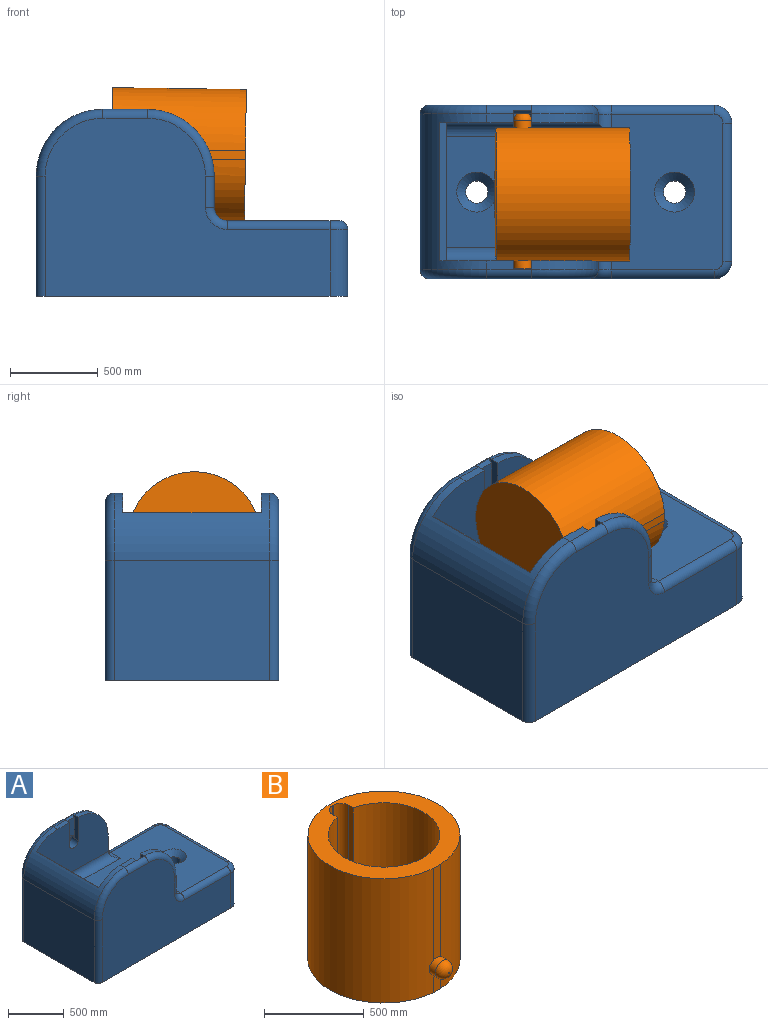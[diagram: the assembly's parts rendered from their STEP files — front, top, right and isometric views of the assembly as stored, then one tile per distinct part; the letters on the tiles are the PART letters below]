
ASSEMBLY  parts=2 mates=1
PART A: 60 faces, bbox 1817.8x1007.3x1098.2 mm
  f0: cylinder r=381mm len=380.99mm, axis (0,-1,0), area 30273.4mm2, adj f9,f10,f27,f48
  f1: plane 149.86x50.8mm, normal (0,0,1), area 7612.9mm2, adj f12,f14,f21,f47
  f2: cylinder r=381mm len=380.99mm, axis (0,-1,0), area 30273.4mm2, adj f12,f13,f22,f49
  f3: plane 1600.2x889mm, normal (0,0,1), area 1094222.8mm2, adj f33,f34,f35,f36,f37,f40,f41,f54
  f4: plane 889x685.8mm, normal (-1,0,0), area 609676.2mm2, adj f8,f14,f42,f43
  f5: plane 1625.6x1016mm, normal (0,-1,0), area 1156662mm2, adj f8,f38,f42,f44,f46,f48,f50,f52
  f6: plane 787.4x381mm, normal (1,0,0), area 299999.4mm2, adj f8,f38,f39,f58
  f7: plane 1625.6x1016mm, normal (0,1,0), area 1156662mm2, adj f8,f39,f43,f45,f47,f49,f51,f53
  f8: plane 1778x990.6mm, normal (0,0,-1), area 1730413.3mm2, adj f4,f5,f6,f7,f19,f20,f38,f39
  f9: plane 965.2x558.8mm, normal (0,1,0), area 450495.6mm2, adj f0,f10,f11,f14,f26,f27,f30,f31
  f10: plane 177.8x50.8mm, normal (1,0,0), area 9032.2mm2, adj f0,f9,f33,f50
  f11: plane 149.86x50.8mm, normal (0,0,1), area 7612.9mm2, adj f9,f14,f26,f46
  f12: plane 965.2x558.8mm, normal (0,-1,0), area 450606.9mm2, adj f1,f2,f13,f14,f17,f21,f22,f30
  f13: plane 177.8x50.8mm, normal (1,0,0), area 9032.2mm2, adj f2,f12,f34,f51
  f14: cylinder r=381mm len=889mm, axis (0,1,0), area 296423.9mm2, adj f1,f4,f9,f11,f12,f32,f44,f45
  f15: cylinder r=53.34mm len=106.68mm, axis (0,1,0), area 12769mm2, adj f16,f28,f29
  f16: plane 106.68x106.68mm, normal (0,1,0), area 8938.3mm2, adj f15
  f17: cylinder r=53.34mm len=106.68mm, axis (0,-1,0), area 21281.7mm2, adj f12,f18,f21,f22,f23
  f18: plane 106.68x106.68mm, normal (0,-1,0), area 8938.3mm2, adj f17
  f19: cylinder r=63.5mm len=381mm, axis (0,0,1), area 152012.2mm2, adj f8,f41
  f20: cylinder r=63.5mm len=381mm, axis (0,0,1), area 152012.2mm2, adj f8,f40
  f21: plane 254x71.7mm, normal (1,0,0), area 13184.9mm2, adj f1,f12,f17,f23,f25,f47
  f22: plane 254x71.71mm, normal (-1,0,0), area 13184.5mm2, adj f2,f12,f17,f23,f24,f49
  f23: plane 228.6x106.68mm, normal (0,-1,0), area 19917.9mm2, adj f17,f21,f22,f24,f25
  f24: cone r=355.6mm half-angle=45deg, axis (0,1,0), area 75.1mm2, adj f22,f23,f25,f49
  f25: plane 104.14x20.9mm, normal (0,-0.71,0.71), area 3078.2mm2, adj f21,f23,f24,f47
  f26: plane 255.04x50.8mm, normal (1,0,0), area 12956.2mm2, adj f9,f11,f28,f29,f59
  f27: plane 255.03x50.8mm, normal (-1,0,0), area 12955.7mm2, adj f0,f9,f28,f29,f59
  f28: plane 254x106.68mm, normal (0,1,0), area 22627.6mm2, adj f15,f26,f27,f46,f48
  f29: plane 106.68x54.38mm, normal (0,1,0), area 111.2mm2, adj f15,f26,f27,f59
  f30: plane 787.4x177.8mm, normal (1,0,0), area 139999.7mm2, adj f9,f12,f31,f37
  f31: cylinder r=330.34mm len=787.4mm, axis (0,1,0), area 205697.3mm2, adj f9,f12,f30,f32
  f32: plane 787.4x37.23mm, normal (0.68,0,0.73), area 39999.9mm2, adj f9,f12,f14,f31
  f33: cylinder r=76.2mm len=127mm, axis (0,1,0), area 9394.8mm2, adj f3,f10,f35,f52
  f34: cylinder r=76.2mm len=127mm, axis (0,1,0), area 9394.8mm2, adj f3,f13,f36,f53
  f35: cylinder r=76.2mm len=1041.4mm, axis (-1,0,0), area 115529.3mm2, adj f3,f9,f33,f37
  f36: cylinder r=76.2mm len=1041.4mm, axis (1,0,0), area 115529.3mm2, adj f3,f12,f34,f37
  f37: cylinder r=76.2mm len=787.4mm, axis (0,1,0), area 87619mm2, adj f3,f30,f35,f36
  f38: cylinder r=101.6mm len=381mm, axis (0,0,-1), area 60804.9mm2, adj f5,f6,f8,f56
  f39: cylinder r=101.6mm len=381mm, axis (0,0,1), area 60804.9mm2, adj f6,f7,f8,f57
  f40: cone r=63.5mm half-angle=45deg, axis (0,0,1), area 40129.2mm2, adj f3,f20
  f41: cone r=63.5mm half-angle=45deg, axis (0,0,1), area 40129.2mm2, adj f3,f19
  f42: cylinder r=50.8mm len=685.8mm, axis (0,0,1), area 54724.4mm2, adj f4,f5,f8,f44
  f43: cylinder r=50.8mm len=685.8mm, axis (0,0,-1), area 54724.4mm2, adj f4,f7,f8,f45
  f44: torus R=330.2mm, axis (0,1,0), area 45442.2mm2, adj f5,f14,f42,f46
  f45: torus R=330.2mm, axis (0,1,0), area 45442.2mm2, adj f7,f14,f43,f47
  f46: cylinder r=50.8mm len=254mm, axis (-1,0,0), area 20268.3mm2, adj f5,f11,f28,f44,f48
  f47: cylinder r=50.8mm len=254mm, axis (1,0,0), area 18025mm2, adj f1,f7,f21,f25,f45,f49
  f48: torus R=330.2mm, axis (0,1,0), area 45442.2mm2, adj f0,f5,f28,f46,f50
  f49: torus R=330.2mm, axis (0,1,0), area 45387.5mm2, adj f2,f7,f22,f24,f47,f51
  f50: cylinder r=50.8mm len=177.8mm, axis (0,0,-1), area 14187.8mm2, adj f5,f10,f48,f52
  f51: cylinder r=50.8mm len=177.8mm, axis (0,0,-1), area 14187.8mm2, adj f7,f13,f49,f53
  f52: torus R=127mm, axis (0,1,0), area 11865mm2, adj f5,f33,f50,f54
  f53: torus R=127mm, axis (0,1,0), area 11865mm2, adj f7,f34,f51,f55
  f54: cylinder r=50.8mm len=584.2mm, axis (-1,0,0), area 46617.1mm2, adj f3,f5,f52,f56
  f55: cylinder r=50.8mm len=584.2mm, axis (1,0,0), area 46617.1mm2, adj f3,f7,f53,f57
  f56: torus R=50.8mm, axis (0,0,1), area 10421.1mm2, adj f3,f38,f54,f58
  f57: torus R=50.8mm, axis (0,0,1), area 10421.1mm2, adj f3,f39,f55,f58
  f58: cylinder r=50.8mm len=787.4mm, axis (0,-1,0), area 62831.7mm2, adj f3,f6,f56,f57
  f59: cylinder r=53.34mm len=106.68mm, axis (0,-1,0), area 8512.7mm2, adj f9,f26,f27,f29
PART B: 25 faces, bbox 762x937.2x762 mm
  f0: plane 762x760.99mm, normal (0,0,1), area 202317.2mm2, adj f1,f2,f5,f8,f10,f12,f13,f20
  f1: cylinder r=381mm len=762mm, axis (0,0,-1), area 861356.5mm2, adj f0,f3,f6,f9,f12,f13,f14,f15
  f2: cylinder r=381mm len=762mm, axis (0,0,-1), area 878934.3mm2, adj f0,f4,f5,f7,f8,f9,f14,f15
  f3: plane 108.41x50.8mm, normal (0,-1,0), area 5273.3mm2, adj f1,f4,f9,f15
  f4: plane 108.41x0.77mm, normal (-1,0,0), area 83.3mm2, adj f2,f3,f9,f15
  f5: plane 565.61x0.77mm, normal (-1,0,0), area 434.7mm2, adj f0,f2,f13,f15
  f6: plane 108.41x50.8mm, normal (0,1,0), area 5273.3mm2, adj f1,f7,f9,f14
  f7: plane 108.41x0.77mm, normal (-1,0,0), area 83.3mm2, adj f2,f6,f9,f14
  f8: plane 565.61x0.77mm, normal (-1,0,0), area 434.7mm2, adj f0,f2,f12,f14
  f9: plane 762x760.99mm, normal (0,0,-1), area 455940.2mm2, adj f1,f2,f3,f4,f6,f7
  f10: cylinder r=279.4mm len=711.2mm, axis (0,0,1), area 1166659.3mm2, adj f0,f11,f20,f21
  f11: plane 641.79x558.8mm, normal (0,0,1), area 253623mm2, adj f10,f20,f21,f22,f23,f24
  f12: plane 565.61x50.8mm, normal (0,1,0), area 28499mm2, adj f0,f1,f8,f14
  f13: plane 565.61x50.8mm, normal (0,-1,0), area 28499mm2, adj f0,f1,f5,f15
  f14: cylinder r=50.8mm len=101.6mm, axis (0,-1,0), area 13220.8mm2, adj f1,f2,f6,f7,f8,f12,f17
  f15: cylinder r=50.8mm len=101.6mm, axis (0,1,0), area 13220.8mm2, adj f1,f2,f3,f4,f5,f13,f19
  f16: plane 5.08x5.08mm, normal (0,1,0), area 20.3mm2, adj f17
  f17: torus R=2.54mm, axis (0,1,0), area 15843.5mm2, adj f14,f16
  f18: plane 5.08x5.08mm, normal (0,-1,0), area 20.3mm2, adj f19
  f19: torus R=2.54mm, axis (0,-1,0), area 15843.5mm2, adj f15,f18
  f20: plane 711.2x33.16mm, normal (1,0,0), area 23582.8mm2, adj f0,f10,f11,f24
  f21: plane 711.2x33.16mm, normal (-1,0,0), area 23582.8mm2, adj f0,f10,f11,f22
  f22: cylinder r=55.74mm len=711.2mm, axis (0,0,1), area 62270.9mm2, adj f0,f11,f21,f23
  f23: plane 711.2x2.82mm, normal (0,-1,0), area 2004.4mm2, adj f0,f11,f22,f24
  f24: cylinder r=55.74mm len=711.2mm, axis (0,0,1), area 62270.9mm2, adj f0,f11,f20,f23
PLACE A t=(-856.57,0,181.73)mm
PLACE B rot(axis=(0,1,0),90.8deg) t=(-1021.88,188.54,937.41)mm
MATE revolute B.f14 <-> A.f15  axis (0,-1,0) through (-868.68,-295.87,994.53)mm
